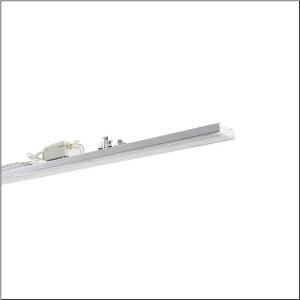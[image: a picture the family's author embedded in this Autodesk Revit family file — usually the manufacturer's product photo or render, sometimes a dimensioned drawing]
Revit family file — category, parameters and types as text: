
# Revit family: licross_r__21_recessed_ho_52tl12dv4l2md_9758
name_source: partatom
category: Lighting Fixtures
units: mm (PartAtom-declared; Revit-internal decimal feet)

## family parameters
Cut with Voids When Loaded = No
Host = Face
Light Source = No
Part Type = Normal
Room Calculation Point = No
Round Connector Dimension = Use Diameter
Shared = No

## types (1)
- --- (1 x LED, 22710 lm, 125.6 W, 4000K)
    Apparent Load = 126 VA
    CIE Flux Codes = 69 91 98 100 100
    Color Rendering = 80
    Color Temperature = 4000K
    Default Elevation = 1800 mm
    Description = Licross® 21 Recessed HO, luminaire insert, of sheet steel, galvanised, coil coated, white, length: 2.250mm, width: 66mm, height: 67mm, LED rated luminous flux: 22.710lm, light colour: 840, control gear: DALI 2, with plug, 6-pole, with phase selection, mains connection: 220..240V, AC/DC, 0/50..60Hz, rated input power: 126W, without changeover relay, for emergency light function, for central battery installations according to DIN EN 60598-2-22, halogen-free wiring, primary optical cover: cover, of PMMA, light emission: direct distribution, primary light characteristic: symmetric, protection rating (complete): IP40, insulation class (complete): insulation class I (protective earthing), certification: CE, ENEC, VDE, UKCA, protection symbol: D if used in an environment without relevant dust loads with corresponding accessories, impact resistance: IK06, permissible ambient temperature for indoor applications: -40..+30°C, standard: EN 60598-2-22, corresponds to IFS (International Featured Standards) requirements for safety and quality in the food industry, reducing of maximum allowable ambient temperature of 5°C with ceiling mounting, LABS conformity tested according to VDMA 24364:2018-05, packaging unit: 1 piece
    Height = 58 mm
    Lamp = 1 x LED
    Lamp Light Flux = 22710 lm
    Lamp Power = 125.6 W
    Lamp count = 1
    Length = 2250 mm
    Luminous efficacy = 181 lm/W
    Manufacturer = Siteco
    ModVariant = No
    Model = 52TL12DV4L2MD
    Mounting Place = Ceiling
    Mounting Type = Pendant
    Number of Poles = 1
    OnlyDefault = Yes
    Power Factor = 1
    Product Name = Licross® 21 Recessed HO
    Product group = luminaire insert
    ProductGroupID = 901
    Protection Class = Protection class I
    Protection Degree = IP 40
    RLX_Detail_Level = 1
    RLX_Emergency_Light_Flux = 0 lm
    RLX_Emergency_Type = 0
    RLX_Emergency_Type_DB = No
    RlxData = <blob elided: 29961 chars, md5=d674c6d5>
    Socket = socket
    Standby Power = 0 W
    System Light Flux = 22710 lm
    System Power = 126 W
    Type Comments = : AC-mode, luminous flux: 100 % | dim-lin: 254 | 489 mA
    Type Image = l_1296930.jpg
    URL = http://relux.com
    VarID = @adj_041807
    Voltage = 0 V
    Weight = 0.00 kg
    Width = 66 mm

## geometry (parser evidence)
native form markers: Blend x4, Sweep x9
no freeform markers — native parametric forms only
